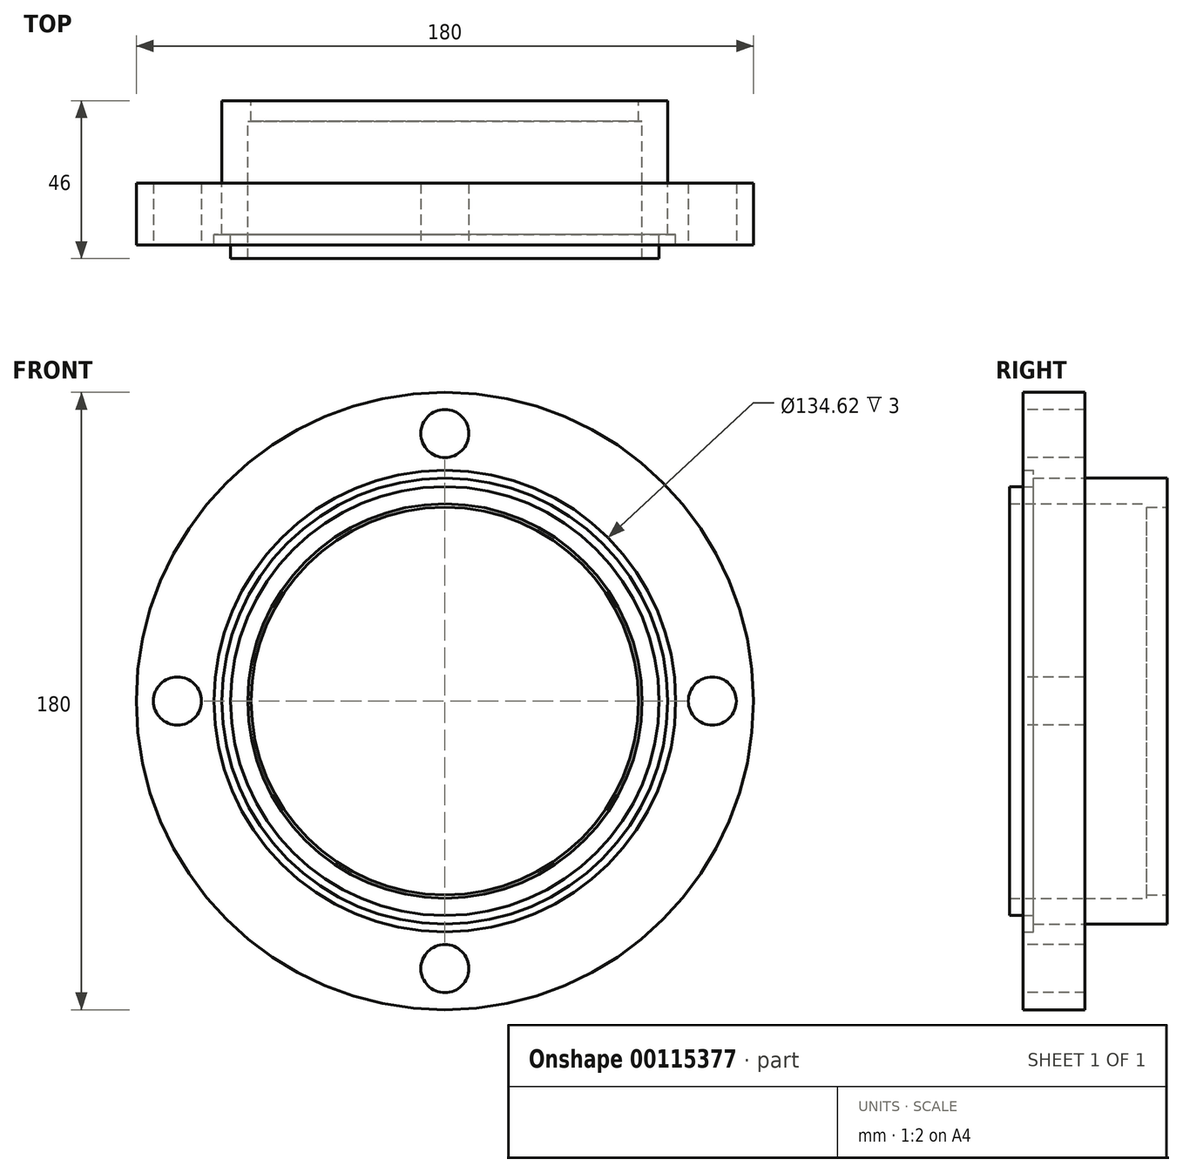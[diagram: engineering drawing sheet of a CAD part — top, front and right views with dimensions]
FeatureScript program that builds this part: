
annotation { "Feature Type Name" : "Feature", "Feature Type Description" : "" }
export const myFeature = defineFeature(function(context is Context, id is Id, definition is map)
    precondition{}
    {
        {
            var Q0;
            Q0=qCreatedBy(makeId("Front.planeOp"),FACE);
            var sketch = newSketch(context, id + "F0", { "sketchPlane" : qUnion([Q0])});
            skCircle(sketch, "E0", {"center": v(0, 0) * mm, "radius": 56.5 * mm});
            skCircle(sketch, "E1", {"center": v(0, 0) * mm, "radius": 65 * mm});
            skSolve(sketch);
        }
        {
            var Q0;
            Q0=makeQuery(id+"F0.imprint","IMPRINT",FACE,{"disambiguationData":[TD([[makeQuery(id+"F0.imprint","IMPRINT",EDGE,{"derivedFrom":sQuery(id+"F0.wireOp",EDGE,"E0")}),-1.0]])]});
            extrude(context, id + "F1", {"entities" : qUnion([Q0]), "depth" : 6 * mm, "offsetDistance" : 25 * mm});
        }
        {
            var Q0;
            Q0=makeQuery(id+"F1.opExtrude","CAP_FACE",FACE,{"disambiguationData":[OSD([sQuery(id+"F0.wireOp",EDGE,"E0"),sQuery(id+"F0.wireOp",EDGE,"E1")])],"isStart":false});
            var sketch = newSketch(context, id + "F2", { "sketchPlane" : qUnion([Q0])});
            skCircle(sketch, "E2", {"center": v(0, 0) * mm, "radius": 57.5 * mm});
            skCircle(sketch, "E3", {"center": v(0, 0) * mm, "radius": 65 * mm});
            skSolve(sketch);
        }
        {
            var Q0;
            Q0=makeQuery(id+"F2.imprint","IMPRINT",FACE,{"disambiguationData":[TD([[makeQuery(id+"F2.imprint","IMPRINT",EDGE,{"derivedFrom":sQuery(id+"F2.wireOp",EDGE,"E2")}),-1.0]])]});
            extrude(context, id + "F3", {"entities" : qUnion([Q0]), "operationType" : NewBodyOperationType.ADD, "depth" : 18 * mm, "offsetDistance" : 25 * mm});
        }
        {
            var Q0;
            Q0=makeQuery(id+"F3.opExtrude","CAP_FACE",FACE,{"disambiguationData":[OSD([sQuery(id+"F2.wireOp",EDGE,"E2"),sQuery(id+"F2.wireOp",EDGE,"E3")])],"isStart":false});
            var sketch = newSketch(context, id + "F4", { "sketchPlane" : qUnion([Q0])});
            skCircle(sketch, "E4", {"center": v(0, 0) * mm, "radius": 57.5 * mm});
            skCircle(sketch, "E5", {"center": v(0, 0) * mm, "radius": 90 * mm});
            skSolve(sketch);
        }
        {
            var Q0;
            Q0=makeQuery(id+"F4.imprint","IMPRINT",FACE,{"disambiguationData":[TD([[makeQuery(id+"F4.imprint","IMPRINT",EDGE,{"derivedFrom":sQuery(id+"F4.wireOp",EDGE,"E5")}),1.0]])]});
            extrude(context, id + "F5", {"entities" : qUnion([Q0]), "depth" : 15 * mm, "offsetDistance" : 25 * mm});
        }
        {
            var Q0;
            Q0=makeQuery(id+"F3.opExtrude","CAP_FACE",FACE,{"disambiguationData":[OSD([sQuery(id+"F2.wireOp",EDGE,"E2"),sQuery(id+"F2.wireOp",EDGE,"E3")])],"isStart":false});
            extrude(context, id + "F6", {"entities" : qUnion([Q0]), "depth" : 15 * mm, "offsetDistance" : 25 * mm});
        }
        {
            var Q0;
            Q0=makeQuery(id+"F6.opExtrude","CAP_FACE",FACE,{"disambiguationData":[OSD([sQuery(id+"F2.wireOp",EDGE,"E2"),sQuery(id+"F2.wireOp",EDGE,"E3")])],"isStart":false});
            var sketch = newSketch(context, id + "F7", { "sketchPlane" : qUnion([Q0])});
            skCircle(sketch, "E6", {"center": v(0, 0) * mm, "radius": 67.31 * mm});
            skCircle(sketch, "E7", {"center": v(0, 0) * mm, "radius": 90 * mm});
            skSolve(sketch);
        }
        {
            var Q0;
            Q0 = qSketchRegion(id + "F7", true);
            extrude(context, id + "F8", {"entities" : qUnion([Q0]), "operationType" : NewBodyOperationType.ADD, "depth" : 3 * mm, "offsetDistance" : 25 * mm});
        }
        {
            var Q0;
            Q0=makeQuery(id+"F6.opExtrude","CAP_FACE",FACE,{"disambiguationData":[OSD([sQuery(id+"F2.wireOp",EDGE,"E2"),sQuery(id+"F2.wireOp",EDGE,"E3")])],"isStart":false});
            var sketch = newSketch(context, id + "F9", { "sketchPlane" : qUnion([Q0])});
            skCircle(sketch, "E8", {"center": v(0, 0) * mm, "radius": 57.5 * mm});
            skCircle(sketch, "E9", {"center": v(0, 0) * mm, "radius": 62.5 * mm});
            skSolve(sketch);
        }
        {
            var Q0;
            Q0=makeQuery(id+"F9.imprint","IMPRINT",FACE,{"disambiguationData":[TD([[makeQuery(id+"F9.imprint","IMPRINT",EDGE,{"derivedFrom":sQuery(id+"F9.wireOp",EDGE,"E8")}),-1.0]])]});
            extrude(context, id + "F10", {"entities" : qUnion([Q0]), "operationType" : NewBodyOperationType.ADD, "depth" : 7 * mm, "offsetDistance" : 25 * mm});
        }
        {
            var Q0;
            Q0=makeQuery(id+"F8.opExtrude","CAP_FACE",FACE,{"disambiguationData":[OSD([sQuery(id+"F7.wireOp",EDGE,"E6"),sQuery(id+"F7.wireOp",EDGE,"E7")])],"isStart":false});
            var sketch = newSketch(context, id + "F11", { "sketchPlane" : qUnion([Q0])});
            skCircle(sketch, "E10", {"center": v(0, 0) * mm, "radius": 78 * mm, "construction": true});
            skLineSegment(sketch, "E11.0", {"start": v(-78, 0) * mm, "end": v(0, 78) * mm, "construction": true});
            skLineSegment(sketch, "E11.1", {"start": v(0, 78) * mm, "end": v(78, 0) * mm, "construction": true});
            skLineSegment(sketch, "E11.2", {"start": v(78, 0) * mm, "end": v(0, -78) * mm, "construction": true});
            skLineSegment(sketch, "E11.3", {"start": v(0, -78) * mm, "end": v(-78, 0) * mm, "construction": true});
            skCircle(sketch, "E12", {"center": v(-78, 0) * mm, "radius": 7 * mm});
            skCircle(sketch, "E13", {"center": v(0, 78) * mm, "radius": 7 * mm});
            skCircle(sketch, "E14", {"center": v(78, 0) * mm, "radius": 7 * mm});
            skCircle(sketch, "E15", {"center": v(0, -78) * mm, "radius": 7 * mm});
            skSolve(sketch);
        }
        {
            var Q0;
            Q0=makeQuery(id+"F11.imprint","IMPRINT",FACE,{"disambiguationData":[TD([[makeQuery(id+"F11.imprint","IMPRINT",EDGE,{"derivedFrom":sQuery(id+"F11.wireOp",EDGE,"E12")}),1.0]])]});
            var Q1;
            Q1=makeQuery(id+"F11.imprint","IMPRINT",FACE,{"disambiguationData":[TD([[makeQuery(id+"F11.imprint","IMPRINT",EDGE,{"derivedFrom":sQuery(id+"F11.wireOp",EDGE,"E14")}),1.0]])]});
            var Q2;
            Q2=makeQuery(id+"F11.imprint","IMPRINT",FACE,{"disambiguationData":[TD([[makeQuery(id+"F11.imprint","IMPRINT",EDGE,{"derivedFrom":sQuery(id+"F11.wireOp",EDGE,"E15")}),1.0]])]});
            var Q3;
            Q3=makeQuery(id+"F11.imprint","IMPRINT",FACE,{"disambiguationData":[TD([[makeQuery(id+"F11.imprint","IMPRINT",EDGE,{"derivedFrom":sQuery(id+"F11.wireOp",EDGE,"E13")}),1.0]])]});
            extrude(context, id + "F12", {"entities" : qUnion([Q0, Q1, Q2, Q3]), "operationType" : NewBodyOperationType.REMOVE, "depth" : 0 * mm, "offsetDistance" : 25 * mm, "hasSecondDirection" : true, "secondDirectionBound" : SecondDirectionBoundingType.THROUGH_ALL, "secondDirectionOppositeDirection" : true, "secondDirectionDepth" : 25 * mm});
        }
    });
